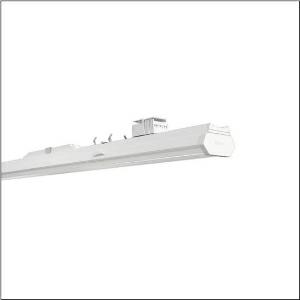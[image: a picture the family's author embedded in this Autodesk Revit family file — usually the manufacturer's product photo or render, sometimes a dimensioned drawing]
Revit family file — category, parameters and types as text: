
# Revit family: licross_r__11_protected_mo_51tp11mn495g_eae0
name_source: partatom
category: Lighting Fixtures
units: mm (PartAtom-declared; Revit-internal decimal feet)

## family parameters
Cut with Voids When Loaded = No
Host = Face
Light Source = No
Part Type = Normal
Room Calculation Point = No
Round Connector Dimension = Use Diameter
Shared = No

## types (1)
- --- (1 x LED, 9980 lm, 55.3 W, 4000K)
    Apparent Load = 55 VA
    CIE Flux Codes = 83 94 98 100 100
    Color Rendering = 80
    Color Temperature = 4000K
    Default Elevation = 1800 mm
    Description = Licross® 11 Protected MO, luminaire insert, of sheet steel, galvanised, coil coated, white, length: 1.500mm, width: 90mm, height: 101mm, LED rated luminous flux: 9.980lm, light colour: 840, control gear: ON/OFF Multilumen, with plug, 3-pole, with phase selection, mains connection: 220..240V, AC, 50/60Hz, rated input power: 55W, halogen-free wiring, primary light control with lens, of plastic, primary optical cover: cover, of PMMA, light emission: direct distribution, primary light characteristic: symmetric, protection rating (complete): IP64, insulation class (complete): insulation class I (protective earthing), certification: CE, ENEC, VDE, UKCA, protection symbol: D if used in an environment with conductive dust loads with corresponding accessories, impact resistance: IK06, permissible ambient temperature for indoor applications: -35..+40°C, corresponds to IFS (International Featured Standards) requirements for safety and quality in the food industry, reducing of maximum allowable ambient temperature of 5°C with ceiling mounting, LABS conformity tested according to VDMA 24364:2018-05, packaging unit: 1 piece
    Height = 92 mm
    Lamp = 1 x LED
    Lamp Light Flux = 9980 lm
    Lamp Power = 55.3 W
    Lamp count = 1
    Length = 1500 mm
    Luminous efficacy = 180 lm/W
    Manufacturer = Siteco
    ModVariant = No
    Model = 51TP11MN495G
    Mounting Place = Ceiling
    Mounting Type = Pendant
    Number of Poles = 1
    OnlyDefault = Yes
    Power Factor = 1
    Product Name = Licross® 11 Protected MO
    Product group = luminaire insert
    ProductGroupID = 902
    Protection Class = Protection class I
    Protection Degree = IP 64
    RLX_Detail_Level = 1
    RLX_Emergency_Light_Flux = 0 lm
    RLX_Emergency_Type = 0
    RLX_Emergency_Type_DB = No
    RlxData = <blob elided: 21805 chars, md5=979768c6>
    Socket = socket
    Standby Power = 0 W
    System Light Flux = 9980 lm
    System Power = 55 W
    Type Comments = factory setting: luminous flux: 100 % | (A | C | E) | 126 mA
    Type Image = l_1256148.jpg
    URL = http://relux.com
    VarID = @adj_085774
    Voltage = 0 V
    Weight = 0.00 kg
    Width = 88 mm

## geometry (parser evidence)
native form markers: Blend x4, Sweep x9
no freeform markers — native parametric forms only
